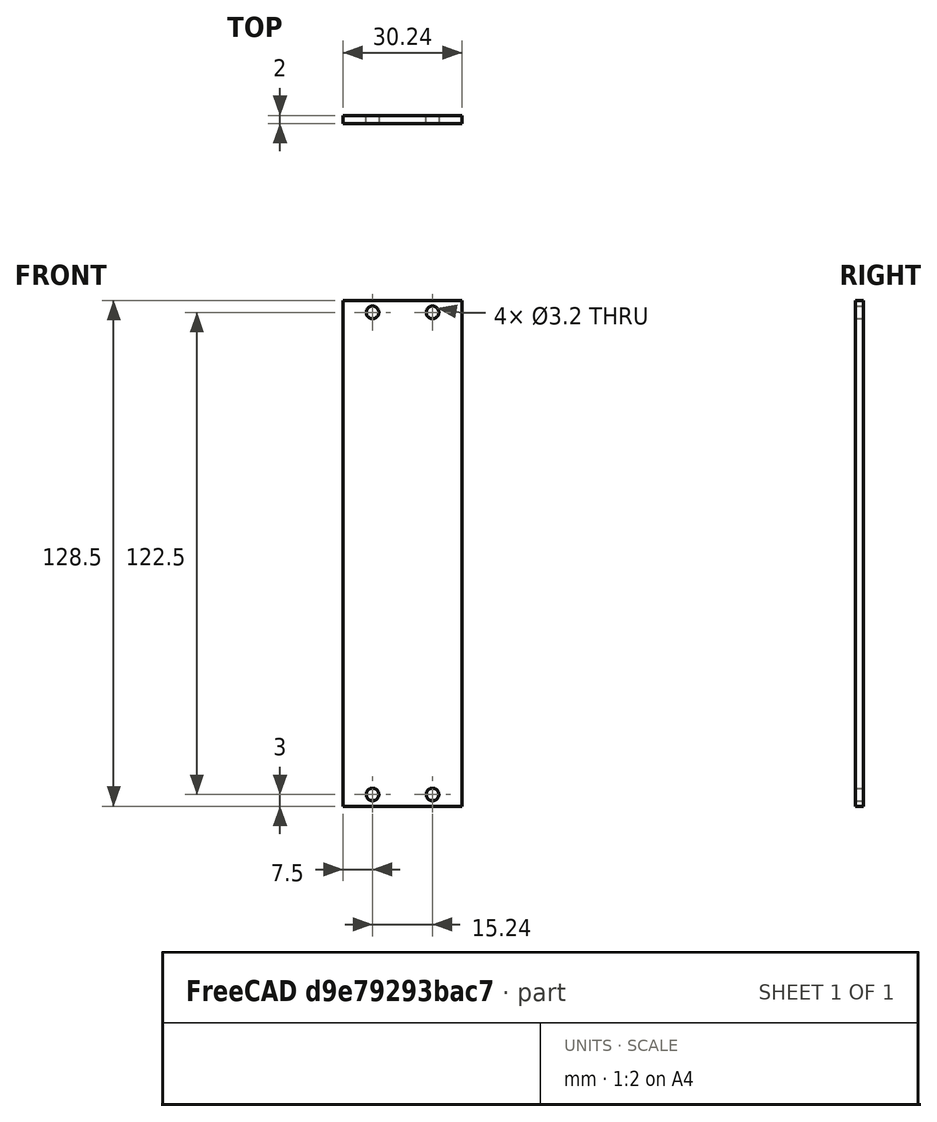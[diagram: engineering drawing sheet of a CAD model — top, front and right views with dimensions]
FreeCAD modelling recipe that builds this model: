
FCSTD DOCUMENT  (FreeCAD 1.0R38641 +678 (Git))
Label: 6hp_plate
License: All rights reserved
LicenseURL: https://en.wikipedia.org/wiki/All_rights_reserved
objects: Sketcher::SketchObject×1, PartDesign::Pad×1, PartDesign::Body×1, App::VarSet×1
note: 6 computed .brp shape members not serialized (recipe doc carries the construction recipe); baked Part::Feature solids carry a one-line shape summary decoded from their .brp
EXTERNAL_REF file=plate_dims.FCStd obj=VarSet

FEATURE [Sketcher::SketchObject] Sketch
  ArcFitTolerance = 1e-06
  AttachmentSupport = -> [XZ_Plane]
  FullyConstrained = true
  MakeInternals = false
  MapMode = 5
  Placement = pos=(0,0,0) rot=(1,0,0;1.5708rad)
  expr: Constraints[39] = <<plate_dims>>#VarSet.HoleOffsetY
  expr: Constraints[40] = <<plate_dims>>#VarSet.HoleOffsetX
  expr: Constraints[48] = <<plate_dims>>#VarSet.HoleDiameter
  expr: Constraints[49] = <<plate_dims>>#VarSet.PlateHeight
  expr: Constraints[52] = <<plate_dims>>#VarSet.HoleSpacing * (VarSet.PlateWidthHP - 3)
  sketch-geometry (20):
    g0: LineSegment StartX=-15.12 StartY=64.25 StartZ=0 EndX=-15.12 EndY=-64.25 EndZ=0
    g1: LineSegment StartX=-15.12 StartY=-64.25 StartZ=0 EndX=15.12 EndY=-64.25 EndZ=0
    g2: LineSegment StartX=15.12 StartY=-64.25 StartZ=0 EndX=15.12 EndY=64.25 EndZ=0
    g3: LineSegment StartX=15.12 StartY=64.25 StartZ=0 EndX=-15.12 EndY=64.25 EndZ=0
    g4: LineSegment [constr] StartX=7.62 StartY=61.25 StartZ=0 EndX=15.12 EndY=61.25 EndZ=0
    g5: LineSegment [constr] StartX=7.62 StartY=64.25 StartZ=0 EndX=7.62 EndY=61.25 EndZ=0
    g6: LineSegment [constr] StartX=7.62 StartY=61.25 StartZ=0 EndX=7.62 EndY=-61.25 EndZ=0
    g7: LineSegment [constr] StartX=7.62 StartY=-61.25 StartZ=0 EndX=7.62 EndY=-64.25 EndZ=0
    g8: LineSegment [constr] StartX=7.62 StartY=-61.25 StartZ=0 EndX=15.12 EndY=-61.25 EndZ=0
    g9: LineSegment [constr] StartX=-7.62 StartY=-61.25 StartZ=0 EndX=-7.62 EndY=-64.25 EndZ=0
    g10: LineSegment [constr] StartX=-15.12 StartY=-61.25 StartZ=0 EndX=-7.62 EndY=-61.25 EndZ=0
    g11: LineSegment [constr] StartX=-7.62 StartY=-61.25 StartZ=0 EndX=7.62 EndY=-61.25 EndZ=0
    g12: LineSegment [constr] StartX=-15.12 StartY=61.25 StartZ=0 EndX=-7.62 EndY=61.25 EndZ=0
    g13: LineSegment [constr] StartX=-7.62 StartY=61.25 StartZ=0 EndX=7.62 EndY=61.25 EndZ=0
    g14: LineSegment [constr] StartX=-7.62 StartY=64.25 StartZ=0 EndX=-7.62 EndY=61.25 EndZ=0
    g15: LineSegment [constr] StartX=-7.62 StartY=61.25 StartZ=0 EndX=-7.62 EndY=-61.25 EndZ=0
    g16: Circle CenterX=-7.62 CenterY=61.25 CenterZ=0 NormalX=0 NormalY=0 NormalZ=1 AngleXU=0 Radius=1.6
    g17: Circle CenterX=7.62 CenterY=61.25 CenterZ=0 NormalX=0 NormalY=0 NormalZ=1 AngleXU=0 Radius=1.6
    g18: Circle CenterX=7.62 CenterY=-61.25 CenterZ=0 NormalX=0 NormalY=0 NormalZ=1 AngleXU=0 Radius=1.6
    g19: Circle CenterX=-7.62 CenterY=-61.25 CenterZ=0 NormalX=0 NormalY=0 NormalZ=1 AngleXU=0 Radius=1.6
  constraints (58):
    c: Coincident(g0,g1)
    c: Coincident(g1,g2)
    c: Coincident(g2,g3)
    c: Coincident(g3,g0)
    c: Vertical(g2)
    c: Horizontal(g1)
    c: PointOnObject(g14,g3)
    c: PointOnObject(g9,g1)
    c: PointOnObject(g12,g0)
    c: PointOnObject(g4,g2)
    c: PointOnObject(g10,g0)
    c: PointOnObject(g8,g2)
    c: PointOnObject(g5,g3)
    c: PointOnObject(g7,g1)
    c: Coincident(g13,g4)
    c: Horizontal(g4)
    c: Coincident(g5,g6)
    c: Vertical(g5)
    c: Coincident(g6,g7)
    c: Vertical(g6)
    c: Vertical(g7)
    c: Coincident(g11,g8)
    c: Horizontal(g8)
    c: Coincident(g15,g9)
    c: Vertical(g9)
    c: Coincident(g10,g11)
    c: Horizontal(g10)
    c: Horizontal(g11)
    c: Coincident(g12,g13)
    c: Horizontal(g12)
    c: Horizontal(g13)
    c: Coincident(g14,g15)
    c: Vertical(g14)
    c: Vertical(g15)
    c: Coincident(g12,g14)
    c: Coincident(g9,g10)
    c: Coincident(g8,g6)
    c: Coincident(g4,g5)
    c: Equal(g9,g14)
    c: Distance(g9,g9) = 3
    c: Distance(g10,g10) = 7.5
    c: Coincident(g16,g12)
    c: Coincident(g17,g4)
    c: Coincident(g18,g6)
    c: Coincident(g19,g9)
    c: Equal(g19,g18)
    c: Equal(g18,g17)
    c: Equal(g17,g16)
    c: Diameter(g16) = 3.2
    c: DistanceY(g0,g0) = 128.5
    c: Distance(g12,g9) = 125.5
    c: Distance(g14,g14) = 3
    c: Distance(g11,g11) = 15.24
    c: Distance(g1,g1) = 30.24
    c: Symmetric(g0,g2,g-2)
    c: Symmetric(g0,g0,g-1)
    c: Distance(g8,g8) = 7.5
    c: Equal(g8,g10)
FEATURE [PartDesign::Pad] Pad
  Direction = (0,-1,2e-16)
  Length = 2
  Length2 = 10
  Placement = pos=(0,0,0) rot=(1,0,0;1.5708rad)
  Profile = -> Sketch
  ReferenceAxis = -> Sketch [N_Axis]
  Refine = true
  Suppressed = false
  Type = 0
  expr: Length = <<plate_dims>>#VarSet.PlateThickness
FEATURE [PartDesign::Body] Body  label="6HpPlate"
  AllowCompound = false
  Group = -> [Sketch,Pad]
  Origin = -> Origin
  Tip = -> Pad
FEATURE [App::VarSet] VarSet
  PlateWidthHP = 6
